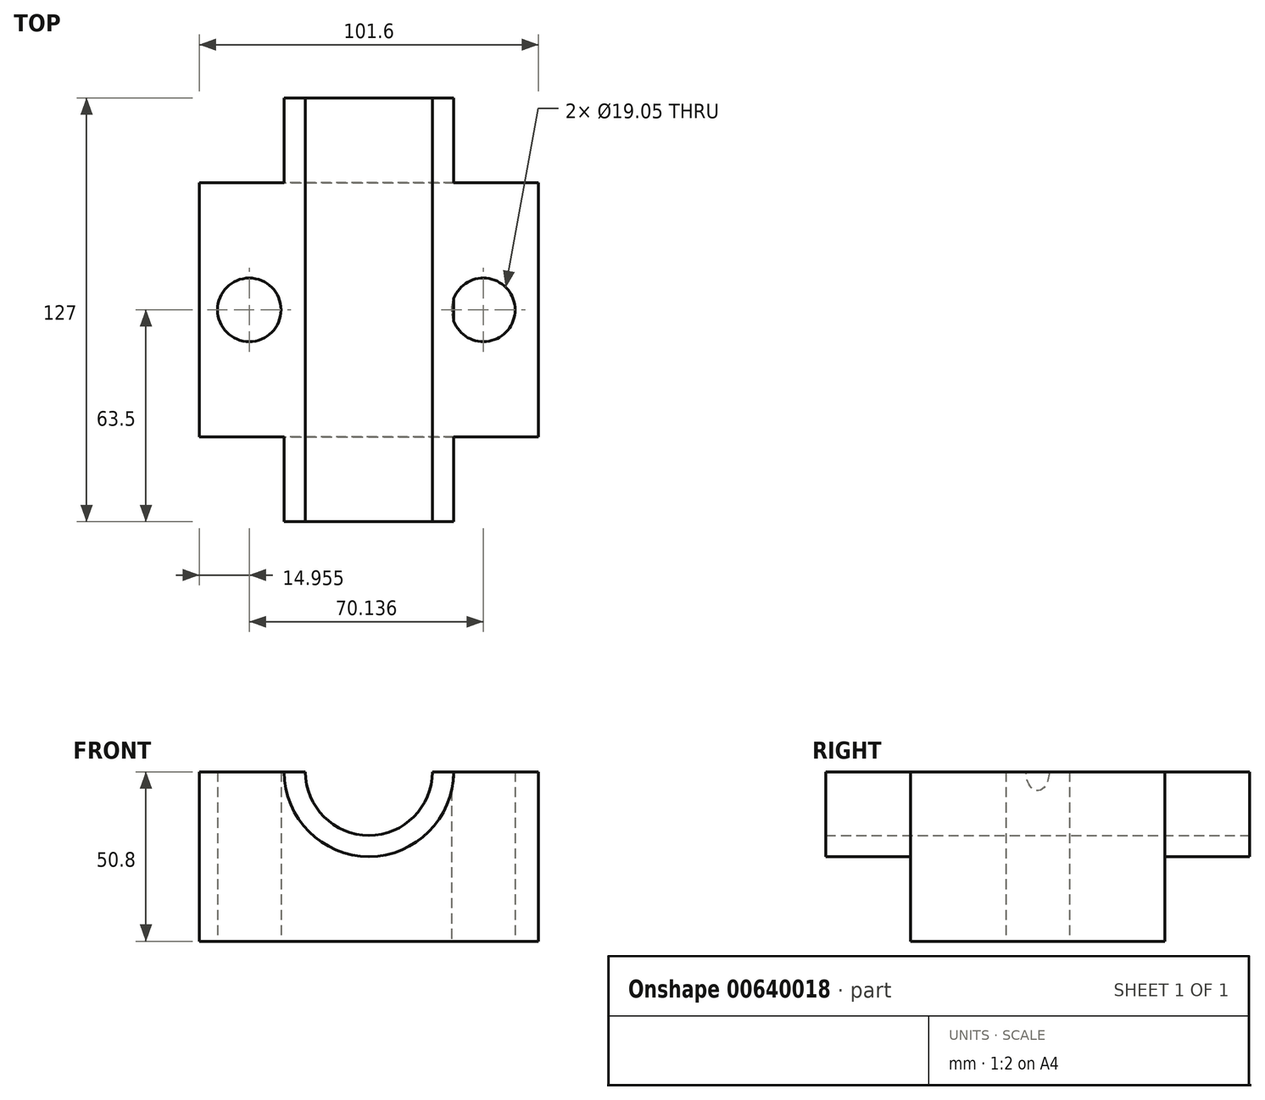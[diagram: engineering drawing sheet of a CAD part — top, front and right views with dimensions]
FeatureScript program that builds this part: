
annotation { "Feature Type Name" : "Feature", "Feature Type Description" : "" }
export const myFeature = defineFeature(function(context is Context, id is Id, definition is map)
    precondition{}
    {
        {
            var Q0;
            Q0=qCreatedBy(makeId("Top.planeOp"),FACE);
            var sketch = newSketch(context, id + "F0", { "sketchPlane" : qUnion([Q0])});
            skLineSegment(sketch, "E0.bottom", {"start": v(-62.76, 0) * mm, "end": v(38.84, 0) * mm});
            skLineSegment(sketch, "E0.top", {"start": v(-62.76, 76.2) * mm, "end": v(38.84, 76.2) * mm});
            skLineSegment(sketch, "E0.left", {"start": v(-62.76, 0) * mm, "end": v(-62.76, 76.2) * mm});
            skLineSegment(sketch, "E0.right", {"start": v(38.84, 0) * mm, "end": v(38.84, 76.2) * mm});
            skCircle(sketch, "E1", {"center": v(-47.8, 38.1) * mm, "radius": 9.53 * mm});
            skPoint(sketch, "E1.centerSnap0", {"position": v(-62.76, 38.1) * mm});
            skCircle(sketch, "E2", {"center": v(22.33, 38.1) * mm, "radius": 9.53 * mm});
            skPoint(sketch, "E2.centerSnap0", {"position": v(38.84, 38.1) * mm});
            skSolve(sketch);
        }
        {
            var Q0;
            Q0=makeQuery(id+"F0.imprint","IMPRINT",FACE,{"disambiguationData":[TD([[makeQuery(id+"F0.imprint","IMPRINT",EDGE,{"derivedFrom":sQuery(id+"F0.wireOp",EDGE,"E0.bottom")}),1.0]])]});
            extrude(context, id + "F1", {"entities" : qUnion([Q0]), "depth" : 50.8 * mm, "offsetDistance" : 25.4 * mm});
        }
        {
            var Q0;
            Q0=makeQuery(id+"F1.opExtrude","SWEPT_FACE",FACE,{"disambiguationData":[OSD([sQuery(id+"F0.wireOp",EDGE,"E0.bottom")])]});
            var sketch = newSketch(context, id + "F2", { "sketchPlane" : qUnion([Q0])});
            skCircle(sketch, "E3", {"center": v(-11.96, 50.8) * mm, "radius": 25.4 * mm});
            skCircle(sketch, "E4", {"center": v(-11.96, 50.8) * mm, "radius": 19.05 * mm});
            skSolve(sketch);
        }
        {
            var Q0;
            {var subQ0=sQuery(id+"F2.wireOp",EDGE,"E3");var subQ1=makeQuery(id+"F1.opExtrude","CAP_EDGE",EDGE,{"disambiguationData":[OSD([sQuery(id+"F0.wireOp",EDGE,"E0.bottom")])],"isStart":false});var subQ2=makeQuery(id+"F2.imprint","INTERSECT",VERTEX,{"disambiguationData":[OD(0.0)],"derivedFrom":[subQ1,subQ0]});Q0=makeQuery(id+"F2.imprint","IMPRINT",FACE,{"disambiguationData":[TD([[makeQuery(id+"F2.imprint","IMPRINT",EDGE,{"disambiguationData":[TD([[subQ2,-1.0]])],"derivedFrom":subQ0}),1.0]])]});}
            extrude(context, id + "F3", {"entities" : qUnion([Q0]), "operationType" : NewBodyOperationType.ADD, "depth" : 25.4 * mm, "offsetDistance" : 25.4 * mm, "hasSecondDirection" : true, "secondDirectionOppositeDirection" : true, "secondDirectionDepth" : 101.6 * mm});
        }
        {
            var Q0;
            {var subQ0=sQuery(id+"F0.wireOp",EDGE,"E0.bottom");var subQ3=sQuery(id+"F2.wireOp",EDGE,"E4");Q0=makeQuery(id+"F3.boolean.opBoolean","SPLIT",FACE,{"disambiguationData":[TD([makeQuery(id+"F3.opExtrude","SWEPT_FACE",FACE,{"disambiguationData":[OSD([subQ3])]})])],"derivedFrom":makeQuery(id+"F1.opExtrude","SWEPT_FACE",FACE,{"disambiguationData":[OSD([subQ0])]})});}
            var sketch = newSketch(context, id + "F4", { "sketchPlane" : qUnion([Q0])});
            skCircle(sketch, "E5", {"center": v(-11.96, 50.8) * mm, "radius": 19.05 * mm});
            skSolve(sketch);
        }
        {
            var Q0;
            {var subQ1=sQuery(id+"F2.wireOp",EDGE,"E4");var subQ3=sQuery(id+"F0.wireOp",EDGE,"E0.bottom");var subQ4=makeQuery(id+"F1.opExtrude","CAP_EDGE",EDGE,{"disambiguationData":[OSD([subQ3])],"isStart":false});var subQ5=makeQuery(id+"F3.boolean.opBoolean","SPLIT",EDGE,{"disambiguationData":[TD([makeQuery(id+"F3.opExtrude","SWEPT_FACE",FACE,{"disambiguationData":[OSD([subQ1])]})])],"derivedFrom":subQ4});Q0=makeQuery(id+"F4.imprint","IMPRINT",FACE,{"disambiguationData":[TD([[makeQuery(id+"F4.imprint","IMPRINT",EDGE,{"derivedFrom":subQ5}),-1.0]])]});}
            var Q1;
            {var subQ1=sQuery(id+"F2.wireOp",EDGE,"E4");var subQ3=sQuery(id+"F0.wireOp",EDGE,"E0.bottom");var subQ4=makeQuery(id+"F1.opExtrude","CAP_EDGE",EDGE,{"disambiguationData":[OSD([subQ3])],"isStart":false});var subQ5=makeQuery(id+"F3.boolean.opBoolean","SPLIT",EDGE,{"disambiguationData":[TD([makeQuery(id+"F3.opExtrude","SWEPT_FACE",FACE,{"disambiguationData":[OSD([subQ1])]})])],"derivedFrom":subQ4});Q1=makeQuery(id+"F4.imprint","IMPRINT",FACE,{"disambiguationData":[TD([[makeQuery(id+"F4.imprint","IMPRINT",EDGE,{"derivedFrom":subQ5}),1.0]])]});}
            extrude(context, id + "F5", {"entities" : qUnion([Q0, Q1]), "operationType" : NewBodyOperationType.REMOVE, "oppositeDirection" : true, "depth" : 76.2 * mm, "offsetDistance" : 25.4 * mm});
        }
    });
